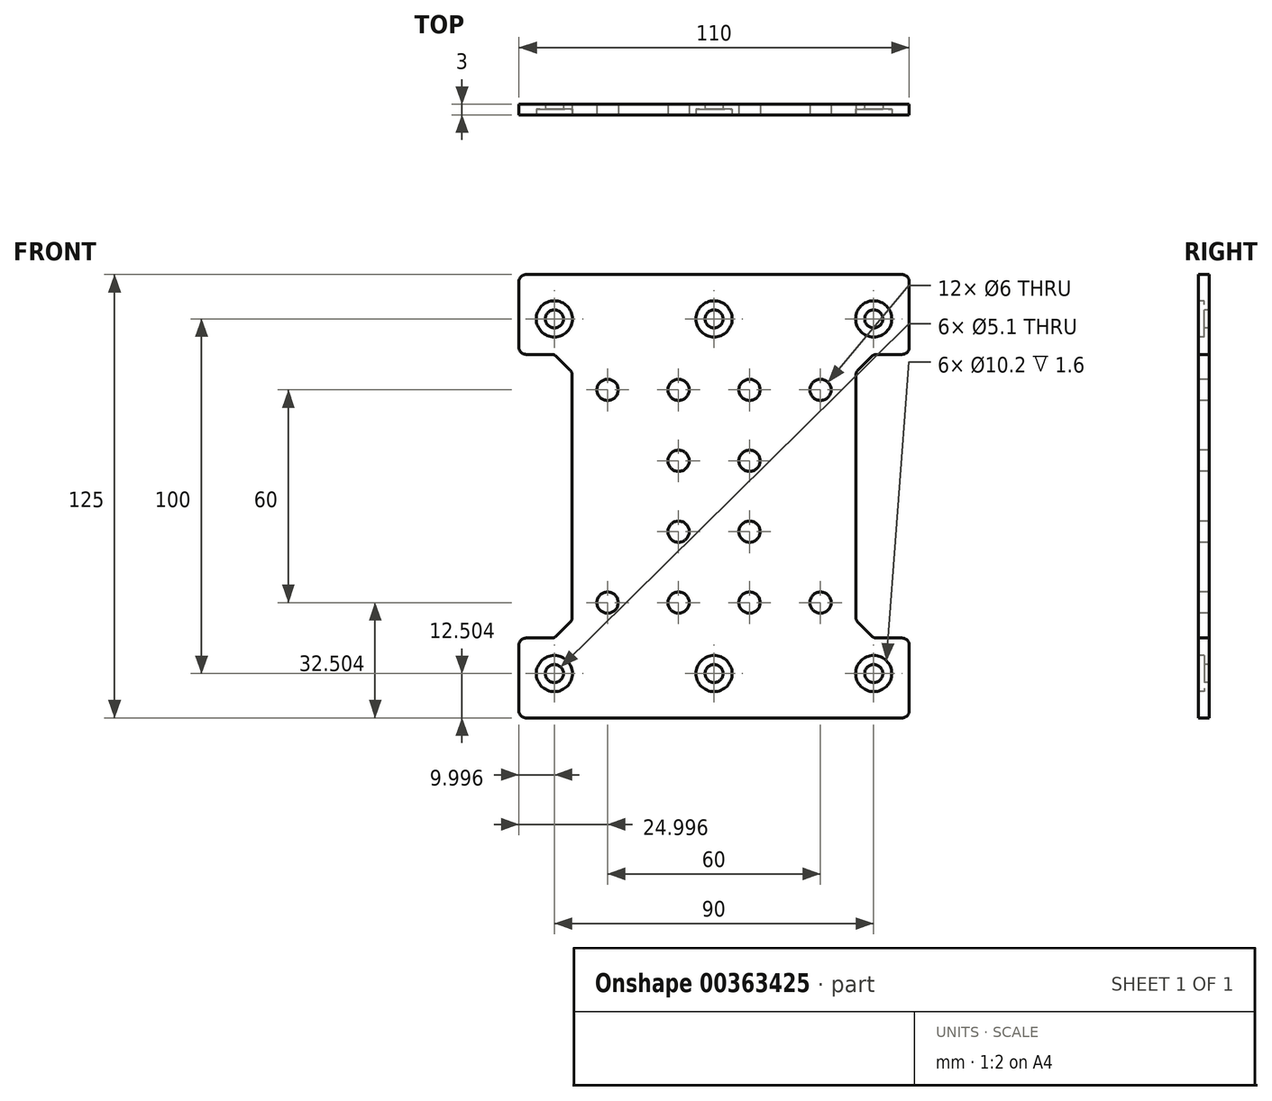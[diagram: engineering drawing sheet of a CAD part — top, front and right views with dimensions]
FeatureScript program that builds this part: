
annotation { "Feature Type Name" : "Feature", "Feature Type Description" : "" }
export const myFeature = defineFeature(function(context is Context, id is Id, definition is map)
    precondition{}
    {
        {
            var Q0;
            Q0=qCreatedBy(makeId("Front.planeOp"),FACE);
            var sketch = newSketch(context, id + "F0", { "sketchPlane" : qUnion([Q0])});
            skLineSegment(sketch, "E0", {"start": v(-210.77, 89) * mm, "end": v(-157.77, 89) * mm});
            skPoint(sketch, "E1", {"position": v(-40, -339.13) * mm});
            skLineSegment(sketch, "E2", {"start": v(-197.77, 26.5) * mm, "end": v(-197.77, 60.75) * mm});
            skLineSegment(sketch, "E3", {"start": v(-203.52, 66.5) * mm, "end": v(-210.77, 66.5) * mm});
            skLineSegment(sketch, "E4", {"start": v(-212.77, 68.5) * mm, "end": v(-212.77, 87) * mm});
            skLineSegment(sketch, "E5", {"start": v(-212.77, 76.5) * mm, "end": v(-157.77, 76.5) * mm, "construction": true});
            skLineSegment(sketch, "E6", {"start": v(-157.77, 89) * mm, "end": v(-157.77, 26.5) * mm});
            skPoint(sketch, "E7", {"position": v(-157.77, 76.5) * mm});
            skPoint(sketch, "E8", {"position": v(-202.77, 76.5) * mm});
            skLineSegment(sketch, "E9", {"start": v(-167.77, 89) * mm, "end": v(-167.77, 26.5) * mm, "construction": true});
            skLineSegment(sketch, "E10", {"start": v(-197.77, 26.5) * mm, "end": v(-157.77, 26.5) * mm});
            skPoint(sketch, "E11", {"position": v(-167.77, 36.5) * mm});
            skPoint(sketch, "E12", {"position": v(-167.77, 56.5) * mm});
            skPoint(sketch, "E13", {"position": v(-187.77, 56.5) * mm});
            skLineSegment(sketch, "E14", {"start": v(-202.25, 65.97) * mm, "end": v(-198.3, 62.02) * mm});
            skPoint(sketch, "E15.visualSharp", {"position": v(-212.77, 66.5) * mm});
            skArc(sketch, "E15.filletArc", {"start": v(-212.77, 68.5) * mm, "mid": v(-212.19, 67.08) * mm, "end": v(-210.77, 66.5) * mm});
            skPoint(sketch, "E16.newPointB", {"position": v(-202.7, 66.41) * mm});
            skArc(sketch, "E16.filletArc", {"start": v(-202.25, 65.97) * mm, "mid": v(-202.83, 66.36) * mm, "end": v(-203.52, 66.5) * mm});
            skPoint(sketch, "E17.newPointB", {"position": v(-197.77, 66.7) * mm});
            skArc(sketch, "E17.filletArc", {"start": v(-197.77, 60.75) * mm, "mid": v(-197.91, 61.44) * mm, "end": v(-198.3, 62.02) * mm});
            skPoint(sketch, "E18.visualSharp", {"position": v(-212.77, 89) * mm});
            skArc(sketch, "E18.filletArc", {"start": v(-210.77, 89) * mm, "mid": v(-212.19, 88.4) * mm, "end": v(-212.77, 87) * mm});
            skSolve(sketch);
        }
        {
            var Q0;
            Q0=makeQuery(id+"F0.imprint","IMPRINT",FACE,{"disambiguationData":[TD([[makeQuery(id+"F0.imprint","IMPRINT",EDGE,{"derivedFrom":sQuery(id+"F0.wireOp",EDGE,"E0")}),-1.0]])]});
            extrude(context, id + "F1", {"entities" : qUnion([Q0]), "oppositeDirection" : true, "depth" : 3 * mm});
        }
        {
            var Q0;
            Q0=sQuery(id+"F0.wireOp",VERTEX,"E13");
            var Q1;
            Q1=sQuery(id+"F0.wireOp",VERTEX,"E12");
            var Q2;
            Q2=sQuery(id+"F0.wireOp",VERTEX,"E11");
            var Q3;
            Q3=makeQuery(id+"F1.opExtrude","SWEPT_BODY",BODY,{"disambiguationData":[OSD([sQuery(id+"F0.wireOp",EDGE,"E0"),sQuery(id+"F0.wireOp",EDGE,"E2"),sQuery(id+"F0.wireOp",EDGE,"E3"),sQuery(id+"F0.wireOp",EDGE,"E4"),sQuery(id+"F0.wireOp",EDGE,"E6"),sQuery(id+"F0.wireOp",EDGE,"E10"),sQuery(id+"F0.wireOp",EDGE,"E14"),sQuery(id+"F0.wireOp",EDGE,"E15.filletArc"),sQuery(id+"F0.wireOp",EDGE,"E16.filletArc"),sQuery(id+"F0.wireOp",EDGE,"E17.filletArc"),sQuery(id+"F0.wireOp",EDGE,"E18.filletArc")])]});
            hole(context, id + "F2", {"style" : HoleStyle.SIMPLE, "endStyle" : HoleEndStyle.BLIND, "holeDiameter" : 6 * mm, "holeDepth" : 34.5 * mm, "isTappedThrough" : true, "tappedDepth" : 30 * mm, "tapClearance" : 3, "startFromSketch" : true, "locations" : qUnion([Q0, Q1, Q2]), "scope" : qUnion([Q3])});
        }
        {
            var Q0;
            Q0=sQuery(id+"F0.wireOp",VERTEX,"E8");
            var Q1;
            Q1=makeQuery(id+"F1.opExtrude","SWEPT_BODY",BODY,{"disambiguationData":[OSD([sQuery(id+"F0.wireOp",EDGE,"E0"),sQuery(id+"F0.wireOp",EDGE,"E2"),sQuery(id+"F0.wireOp",EDGE,"E3"),sQuery(id+"F0.wireOp",EDGE,"E4"),sQuery(id+"F0.wireOp",EDGE,"E6"),sQuery(id+"F0.wireOp",EDGE,"E10"),sQuery(id+"F0.wireOp",EDGE,"E14"),sQuery(id+"F0.wireOp",EDGE,"E15.filletArc"),sQuery(id+"F0.wireOp",EDGE,"E16.filletArc"),sQuery(id+"F0.wireOp",EDGE,"E17.filletArc"),sQuery(id+"F0.wireOp",EDGE,"E18.filletArc")])]});
            hole(context, id + "F3", {"style" : HoleStyle.C_BORE, "endStyle" : HoleEndStyle.BLIND, "holeDiameter" : 5.1 * mm, "cBoreDiameter" : 10.2 * mm, "cBoreDepth" : 1.6 * mm, "holeDepth" : 34.5 * mm, "isTappedThrough" : true, "tappedDepth" : 30 * mm, "tapClearance" : 3, "startFromSketch" : true, "locations" : qUnion([Q0]), "scope" : qUnion([Q1])});
        }
        {
            var Q0;
            Q0=makeQuery(id+"F1.opExtrude","SWEPT_BODY",BODY,{"disambiguationData":[OSD([sQuery(id+"F0.wireOp",EDGE,"E0"),sQuery(id+"F0.wireOp",EDGE,"E2"),sQuery(id+"F0.wireOp",EDGE,"E3"),sQuery(id+"F0.wireOp",EDGE,"E4"),sQuery(id+"F0.wireOp",EDGE,"E6"),sQuery(id+"F0.wireOp",EDGE,"E10"),sQuery(id+"F0.wireOp",EDGE,"E14"),sQuery(id+"F0.wireOp",EDGE,"E15.filletArc"),sQuery(id+"F0.wireOp",EDGE,"E16.filletArc"),sQuery(id+"F0.wireOp",EDGE,"E17.filletArc"),sQuery(id+"F0.wireOp",EDGE,"E18.filletArc")])]});
            var Q1;
            Q1=makeQuery(id+"F1.opExtrude","SWEPT_FACE",FACE,{"disambiguationData":[OSD([sQuery(id+"F0.wireOp",EDGE,"E6")])]});
            mirror(context, id + "F4", {"operationType" : NewBodyOperationType.ADD, "entities" : qUnion([Q0]), "mirrorPlane" : qUnion([Q1])});
        }
        {
            var Q0;
            Q0=sQuery(id+"F0.wireOp",VERTEX,"E7");
            var Q1;
            Q1=makeQuery(id+"F1.opExtrude","SWEPT_BODY",BODY,{"disambiguationData":[OSD([sQuery(id+"F0.wireOp",EDGE,"E0"),sQuery(id+"F0.wireOp",EDGE,"E2"),sQuery(id+"F0.wireOp",EDGE,"E3"),sQuery(id+"F0.wireOp",EDGE,"E4"),sQuery(id+"F0.wireOp",EDGE,"E6"),sQuery(id+"F0.wireOp",EDGE,"E10"),sQuery(id+"F0.wireOp",EDGE,"E14"),sQuery(id+"F0.wireOp",EDGE,"E15.filletArc"),sQuery(id+"F0.wireOp",EDGE,"E16.filletArc"),sQuery(id+"F0.wireOp",EDGE,"E17.filletArc"),sQuery(id+"F0.wireOp",EDGE,"E18.filletArc")])]});
            hole(context, id + "F5", {"style" : HoleStyle.C_BORE, "endStyle" : HoleEndStyle.BLIND, "holeDiameter" : 5.1 * mm, "cBoreDiameter" : 10.2 * mm, "cBoreDepth" : 1.6 * mm, "holeDepth" : 34.5 * mm, "isTappedThrough" : true, "tappedDepth" : 30 * mm, "tapClearance" : 3, "startFromSketch" : true, "locations" : qUnion([Q0]), "scope" : qUnion([Q1])});
        }
        {
            var Q0;
            Q0=makeQuery(id+"F1.opExtrude","SWEPT_BODY",BODY,{"disambiguationData":[OSD([sQuery(id+"F0.wireOp",EDGE,"E0"),sQuery(id+"F0.wireOp",EDGE,"E2"),sQuery(id+"F0.wireOp",EDGE,"E3"),sQuery(id+"F0.wireOp",EDGE,"E4"),sQuery(id+"F0.wireOp",EDGE,"E6"),sQuery(id+"F0.wireOp",EDGE,"E10"),sQuery(id+"F0.wireOp",EDGE,"E14"),sQuery(id+"F0.wireOp",EDGE,"E15.filletArc"),sQuery(id+"F0.wireOp",EDGE,"E16.filletArc"),sQuery(id+"F0.wireOp",EDGE,"E17.filletArc"),sQuery(id+"F0.wireOp",EDGE,"E18.filletArc")])]});
            var Q1;
            {var subQ0=makeQuery(id+"F1.opExtrude","SWEPT_FACE",FACE,{"disambiguationData":[OSD([sQuery(id+"F0.wireOp",EDGE,"E10")])]});Q1=makeQuery(id+"F4.boolean.opBoolean","MERGE",FACE,{"derivedFrom":[subQ0,makeQuery(id+"F4.opPattern","COPY",FACE,{"derivedFrom":subQ0,"instanceName":"1"})]});}
            mirror(context, id + "F6", {"operationType" : NewBodyOperationType.ADD, "entities" : qUnion([Q0]), "mirrorPlane" : qUnion([Q1])});
        }
    });
